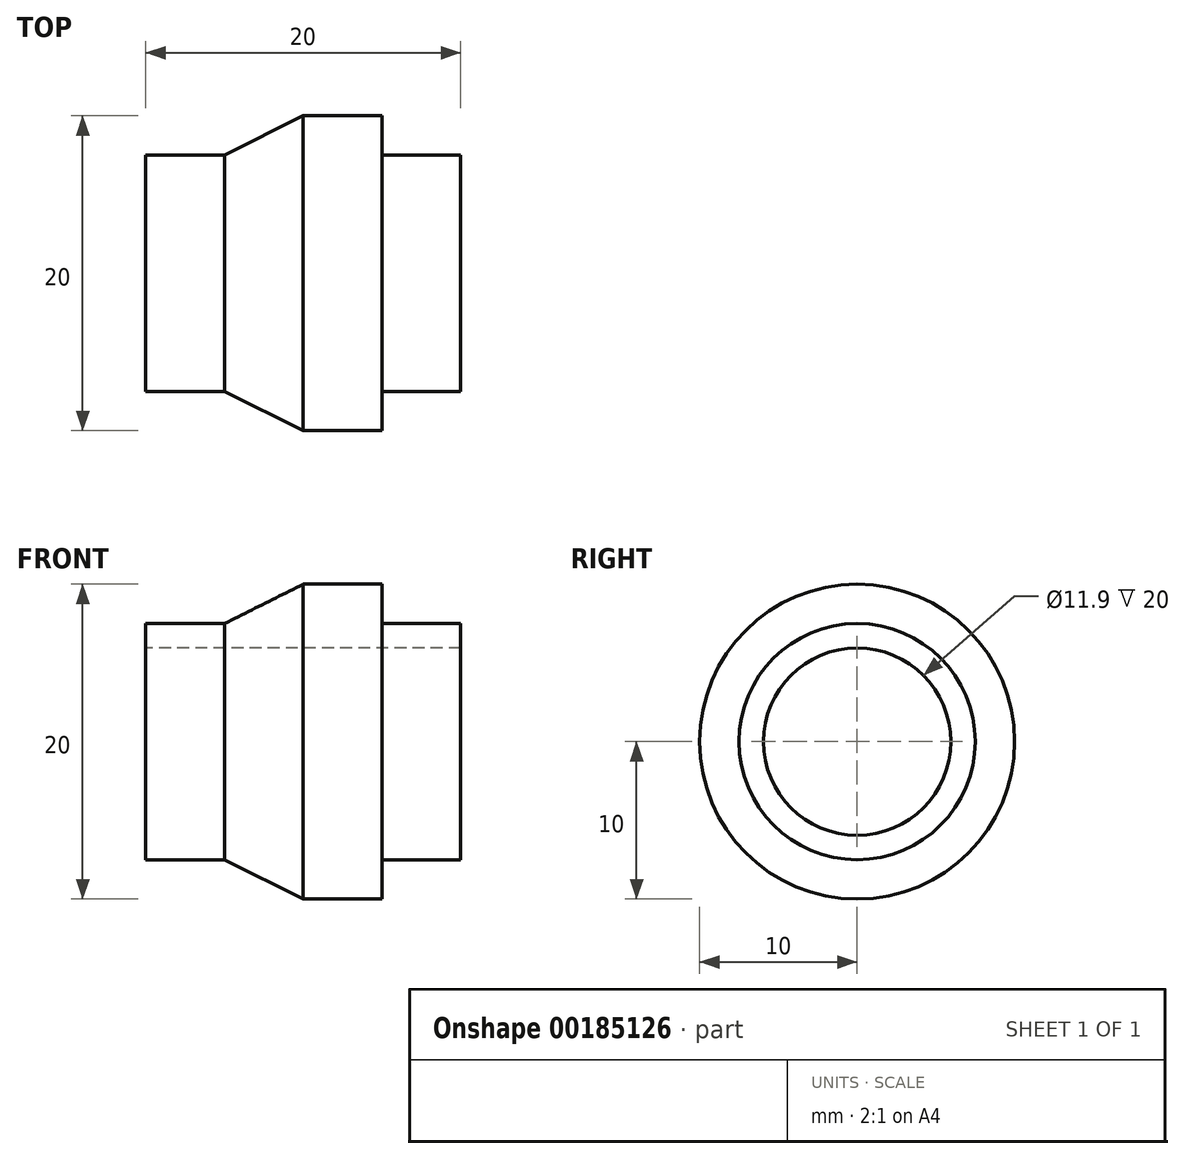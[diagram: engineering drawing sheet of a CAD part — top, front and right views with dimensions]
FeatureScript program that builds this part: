
annotation { "Feature Type Name" : "Feature", "Feature Type Description" : "" }
export const myFeature = defineFeature(function(context is Context, id is Id, definition is map)
    precondition{}
    {
        {
            var Q0;
            Q0=qCreatedBy(makeId("Front.planeOp"),FACE);
            var sketch = newSketch(context, id + "F0", { "sketchPlane" : qUnion([Q0])});
            skLineSegment(sketch, "E0", {"start": v(-53.68, 0) * mm, "end": v(59.34, 0) * mm, "construction": true});
            skLineSegment(sketch, "E1", {"start": v(-20, 5.95) * mm, "end": v(-20, 7.5) * mm});
            skLineSegment(sketch, "E2", {"start": v(-20, 7.5) * mm, "end": v(-15, 7.5) * mm});
            skLineSegment(sketch, "E3", {"start": v(-15, 7.5) * mm, "end": v(-10, 10) * mm});
            skLineSegment(sketch, "E4", {"start": v(-10, 10) * mm, "end": v(-5, 10) * mm});
            skLineSegment(sketch, "E5", {"start": v(-5, 10) * mm, "end": v(-5, 7.5) * mm});
            skLineSegment(sketch, "E6", {"start": v(-5, 7.5) * mm, "end": v(0, 7.5) * mm});
            skLineSegment(sketch, "E7", {"start": v(0, 7.5) * mm, "end": v(0, 5.95) * mm});
            skLineSegment(sketch, "E8", {"start": v(0, 5.95) * mm, "end": v(-20, 5.95) * mm});
            skSolve(sketch);
        }
        {
            var Q0;
            Q0 = qSketchRegion(id + "F0", true);
            var Q1;
            Q1=sQuery(id+"F0.wireOp",EDGE,"E0");
            revolve(context, id + "F1", {"entities" : qUnion([Q0]), "axis" : qUnion([Q1]), "revolveType" : RevolveType.FULL});
        }
    });
